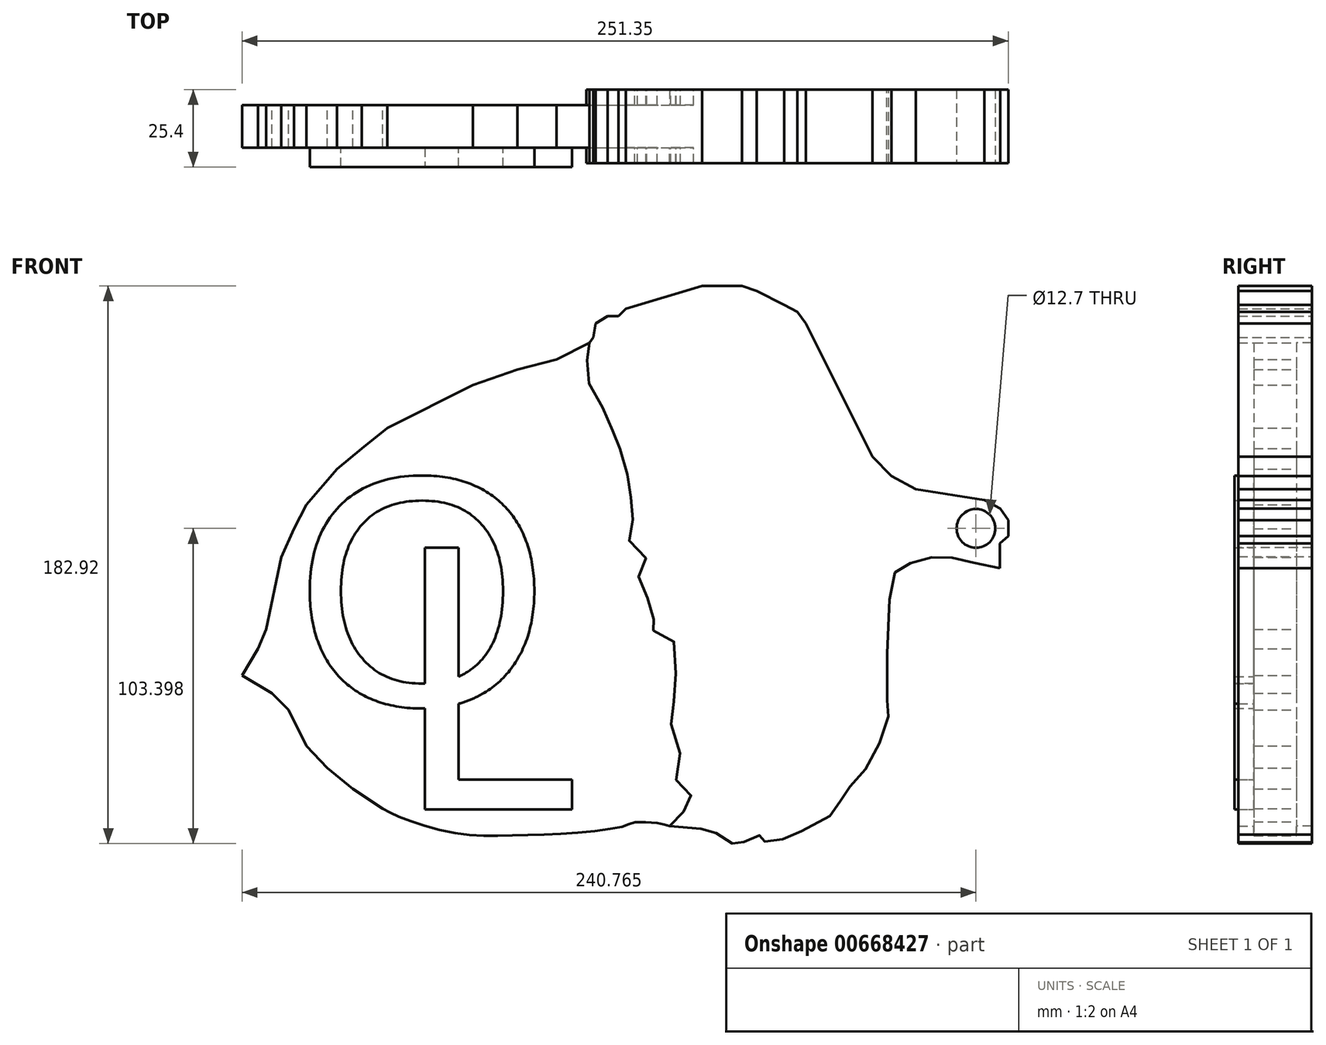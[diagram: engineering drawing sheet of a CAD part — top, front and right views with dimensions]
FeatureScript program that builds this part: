
annotation { "Feature Type Name" : "Feature", "Feature Type Description" : "" }
export const myFeature = defineFeature(function(context is Context, id is Id, definition is map)
    precondition{}
    {
        {
            var Q0;
            Q0=qCreatedBy(makeId("Front.planeOp"),FACE);
            var sketch = newSketch(context, id + "F0", { "sketchPlane" : qUnion([Q0])});
            skLineSegment(sketch, "E0", {"start": v(117.29, -24.43) * mm, "end": v(117.29, -16.31) * mm});
            skLineSegment(sketch, "E1", {"start": v(117.29, -16.31) * mm, "end": v(120, -13.9) * mm});
            skLineSegment(sketch, "E2", {"start": v(120, -13.9) * mm, "end": v(120, -8.7) * mm});
            skLineSegment(sketch, "E3", {"start": v(120, -8.7) * mm, "end": v(117.4, -4.81) * mm});
            skLineSegment(sketch, "E4", {"start": v(117.4, -4.81) * mm, "end": v(112.2, -2.02) * mm});
            skLineSegment(sketch, "E5", {"start": v(112.2, -2.02) * mm, "end": v(89.69, 1.5) * mm});
            skLineSegment(sketch, "E6", {"start": v(89.69, 1.5) * mm, "end": v(81.7, 5.78) * mm});
            skLineSegment(sketch, "E7", {"start": v(81.7, 5.78) * mm, "end": v(75.49, 12.18) * mm});
            skLineSegment(sketch, "E8", {"start": v(75.49, 12.18) * mm, "end": v(53.6, 55.9) * mm});
            skLineSegment(sketch, "E9", {"start": v(53.6, 55.9) * mm, "end": v(50.79, 59.7) * mm});
            skLineSegment(sketch, "E10", {"start": v(50.79, 59.7) * mm, "end": v(46.54, 62.01) * mm});
            skLineSegment(sketch, "E11", {"start": v(46.54, 62.01) * mm, "end": v(37.43, 66.54) * mm});
            skLineSegment(sketch, "E12", {"start": v(37.43, 66.54) * mm, "end": v(32.62, 68.17) * mm});
            skLineSegment(sketch, "E13", {"start": v(32.62, 68.17) * mm, "end": v(25.4, 68.17) * mm});
            skLineSegment(sketch, "E14", {"start": v(25.4, 68.17) * mm, "end": v(19.57, 68.17) * mm});
            skLineSegment(sketch, "E15", {"start": v(19.57, 68.17) * mm, "end": v(-5.42, 60.74) * mm});
            skLineSegment(sketch, "E16", {"start": v(-5.42, 60.74) * mm, "end": v(-7.89, 58.28) * mm});
            skLineSegment(sketch, "E17", {"start": v(-7.89, 58.28) * mm, "end": v(-11.38, 58.28) * mm});
            skLineSegment(sketch, "E18", {"start": v(-11.38, 58.28) * mm, "end": v(-15.33, 55.9) * mm});
            skLineSegment(sketch, "E19", {"start": v(-15.33, 55.9) * mm, "end": v(-16.06, 51.23) * mm});
            skLineSegment(sketch, "E20", {"start": v(-16.06, 51.23) * mm, "end": v(-17.41, 49.45) * mm});
            skLineSegment(sketch, "E21", {"start": v(-17.41, 49.45) * mm, "end": v(-24.9, 45.7) * mm});
            skLineSegment(sketch, "E22", {"start": v(-24.9, 45.7) * mm, "end": v(-28.14, 44.08) * mm});
            skLineSegment(sketch, "E23", {"start": v(-28.14, 44.08) * mm, "end": v(-40.96, 40.7) * mm});
            skLineSegment(sketch, "E24", {"start": v(-40.96, 40.7) * mm, "end": v(-55.61, 35.61) * mm});
            skLineSegment(sketch, "E25", {"start": v(-55.61, 35.61) * mm, "end": v(-66.58, 30.12) * mm});
            skLineSegment(sketch, "E26", {"start": v(-66.58, 30.12) * mm, "end": v(-75.74, 25.53) * mm});
            skLineSegment(sketch, "E27", {"start": v(-75.74, 25.53) * mm, "end": v(-83.63, 21.58) * mm});
            skLineSegment(sketch, "E28", {"start": v(-83.63, 21.58) * mm, "end": v(-92.03, 14.87) * mm});
            skLineSegment(sketch, "E29", {"start": v(-92.03, 14.87) * mm, "end": v(-100.15, 8.05) * mm});
            skLineSegment(sketch, "E30", {"start": v(-100.15, 8.05) * mm, "end": v(-110.16, -3.56) * mm});
            skLineSegment(sketch, "E31", {"start": v(-110.16, -3.56) * mm, "end": v(-114.23, -11.4) * mm});
            skLineSegment(sketch, "E32", {"start": v(-114.23, -11.4) * mm, "end": v(-118.43, -20.82) * mm});
            skLineSegment(sketch, "E33", {"start": v(-118.43, -20.82) * mm, "end": v(-123.37, -44.47) * mm});
            skLineSegment(sketch, "E34", {"start": v(-123.37, -44.47) * mm, "end": v(-126.12, -50.86) * mm});
            skLineSegment(sketch, "E35", {"start": v(-126.12, -50.86) * mm, "end": v(-131.35, -59.56) * mm});
            skLineSegment(sketch, "E36", {"start": v(-131.35, -59.56) * mm, "end": v(-121.57, -65.42) * mm});
            skLineSegment(sketch, "E37", {"start": v(-121.57, -65.42) * mm, "end": v(-116.11, -70.88) * mm});
            skLineSegment(sketch, "E38", {"start": v(-116.11, -70.88) * mm, "end": v(-110.16, -82.76) * mm});
            skLineSegment(sketch, "E39", {"start": v(-110.16, -82.76) * mm, "end": v(-103.34, -89.88) * mm});
            skLineSegment(sketch, "E40", {"start": v(-103.34, -89.88) * mm, "end": v(-94.93, -96.85) * mm});
            skLineSegment(sketch, "E41", {"start": v(-94.93, -96.85) * mm, "end": v(-85.2, -103.23) * mm});
            skFitSpline(sketch, "E42", {"points": [v(-85.2, -103.23) * mm, v(-78.53, -106.42) * mm, v(-60.98, -111.36) * mm, v(-44.15, -112.08) * mm, v(-22.53, -111.21) * mm, v(-5.7, -108.89) * mm, v(-2.36, -107.73) * mm, v(6.49, -108.3) * mm, v(8.96, -109.03) * mm, v(23.03, -110.34) * mm, v(23.76, -110.92) * mm, v(29.12, -114.55) * mm, v(30.57, -114.7) * mm, v(34.2, -113.97) * mm, v(38.4, -111.94) * mm, v(39.14, -111.94) * mm, v(40, -113.97) * mm, v(45.37, -113.53) * mm, v(51.9, -110.77) * mm, v(64.38, -103.23) * mm, v(64.96, -100.18) * mm, v(69.6, -94.53) * mm, v(75.99, -85.68) * mm, v(80.78, -72.47) * mm, v(80.46, -69.35) * mm, v(81.47, -30.75) * mm, v(84.08, -24.66) * mm, v(90.76, -21.76) * mm, v(98.6, -20.6) * mm, v(105.85, -21.9) * mm, v(117.29, -24.43) * mm], "startDerivative": vector(175.5, -94.23) * mm, "endDerivative": vector(297.3, -63.2) * mm});
            skFitSpline(sketch, "E43", {"points": [v(-17.41, 49.45) * mm, v(-17.41, 38.95) * mm, v(-13.96, 29.93) * mm, v(-10.06, 21.27) * mm, v(-8.33, 16.85) * mm, v(-5.5, 7.87) * mm, v(-4.08, 0) * mm, v(-3.31, -7) * mm, v(-3.61, -13.9) * mm, v(0, -20.63) * mm, v(0, -24.43) * mm, v(0, -30.75) * mm, v(3.3, -39.07) * mm, v(2.91, -43.7) * mm, v(6.62, -46.18) * mm, v(10.27, -55.88) * mm, v(10.24, -67.77) * mm, v(9.96, -75.4) * mm, v(11.82, -87.89) * mm, v(12.58, -95.6) * mm, v(14.74, -99.85) * mm, v(8.96, -109.03) * mm], "startDerivative": vector(-16.4, -195.96) * mm, "endDerivative": vector(-157.1, -181.16) * mm});
            skSolve(sketch);
        }
        {
            var Q0;
            Q0=makeQuery(id+"F0.imprint","IMPRINT",FACE,{"disambiguationData":[TD([[makeQuery(id+"F0.imprint","IMPRINT",EDGE,{"derivedFrom":sQuery(id+"F0.wireOp",EDGE,"E21")}),1.0]])]});
            extrude(context, id + "F1", {"entities" : qUnion([Q0]), "depth" : 12.7 * mm, "offsetDistance" : 25.4 * mm});
        }
        {
            var Q0;
            Q0 = qSketchRegion(id + "F0", true);
            var Q1;
            Q1=makeQuery(id+"F1.opExtrude","CAP_FACE",FACE,{"disambiguationData":[OSD([sQuery(id+"F0.wireOp",EDGE,"E21"),sQuery(id+"F0.wireOp",EDGE,"E22"),sQuery(id+"F0.wireOp",EDGE,"E23"),sQuery(id+"F0.wireOp",EDGE,"E24"),sQuery(id+"F0.wireOp",EDGE,"E25"),sQuery(id+"F0.wireOp",EDGE,"E26"),sQuery(id+"F0.wireOp",EDGE,"E27"),sQuery(id+"F0.wireOp",EDGE,"E28"),sQuery(id+"F0.wireOp",EDGE,"E29"),sQuery(id+"F0.wireOp",EDGE,"E30"),sQuery(id+"F0.wireOp",EDGE,"E31"),sQuery(id+"F0.wireOp",EDGE,"E32"),sQuery(id+"F0.wireOp",EDGE,"E33"),sQuery(id+"F0.wireOp",EDGE,"E34"),sQuery(id+"F0.wireOp",EDGE,"E35"),sQuery(id+"F0.wireOp",EDGE,"E36"),sQuery(id+"F0.wireOp",EDGE,"E37"),sQuery(id+"F0.wireOp",EDGE,"E38"),sQuery(id+"F0.wireOp",EDGE,"E39"),sQuery(id+"F0.wireOp",EDGE,"E40"),sQuery(id+"F0.wireOp",EDGE,"E41"),sQuery(id+"F0.wireOp",EDGE,"E42"),sQuery(id+"F0.wireOp",EDGE,"E43")])],"isStart":true});
            extrude(context, id + "F2", {"entities" : qUnion([Q0, Q1]), "operationType" : NewBodyOperationType.ADD, "depth" : 13.97 * mm, "offsetDistance" : 25.4 * mm});
        }
        {
            var Q0;
            Q0=makeQuery(id+"F2.opExtrude","CAP_FACE",FACE,{"disambiguationData":[OSD([sQuery(id+"F0.wireOp",EDGE,"E0"),sQuery(id+"F0.wireOp",EDGE,"E1"),sQuery(id+"F0.wireOp",EDGE,"E2"),sQuery(id+"F0.wireOp",EDGE,"E3"),sQuery(id+"F0.wireOp",EDGE,"E4"),sQuery(id+"F0.wireOp",EDGE,"E5"),sQuery(id+"F0.wireOp",EDGE,"E6"),sQuery(id+"F0.wireOp",EDGE,"E7"),sQuery(id+"F0.wireOp",EDGE,"E8"),sQuery(id+"F0.wireOp",EDGE,"E9"),sQuery(id+"F0.wireOp",EDGE,"E10"),sQuery(id+"F0.wireOp",EDGE,"E11"),sQuery(id+"F0.wireOp",EDGE,"E12"),sQuery(id+"F0.wireOp",EDGE,"E13"),sQuery(id+"F0.wireOp",EDGE,"E14"),sQuery(id+"F0.wireOp",EDGE,"E15"),sQuery(id+"F0.wireOp",EDGE,"E16"),sQuery(id+"F0.wireOp",EDGE,"E17"),sQuery(id+"F0.wireOp",EDGE,"E18"),sQuery(id+"F0.wireOp",EDGE,"E19"),sQuery(id+"F0.wireOp",EDGE,"E20"),sQuery(id+"F0.wireOp",EDGE,"E21"),sQuery(id+"F0.wireOp",EDGE,"E22"),sQuery(id+"F0.wireOp",EDGE,"E23"),sQuery(id+"F0.wireOp",EDGE,"E24"),sQuery(id+"F0.wireOp",EDGE,"E25"),sQuery(id+"F0.wireOp",EDGE,"E26"),sQuery(id+"F0.wireOp",EDGE,"E27"),sQuery(id+"F0.wireOp",EDGE,"E28"),sQuery(id+"F0.wireOp",EDGE,"E29"),sQuery(id+"F0.wireOp",EDGE,"E30"),sQuery(id+"F0.wireOp",EDGE,"E31"),sQuery(id+"F0.wireOp",EDGE,"E32"),sQuery(id+"F0.wireOp",EDGE,"E33"),sQuery(id+"F0.wireOp",EDGE,"E34"),sQuery(id+"F0.wireOp",EDGE,"E35"),sQuery(id+"F0.wireOp",EDGE,"E36"),sQuery(id+"F0.wireOp",EDGE,"E37"),sQuery(id+"F0.wireOp",EDGE,"E38"),sQuery(id+"F0.wireOp",EDGE,"E39"),sQuery(id+"F0.wireOp",EDGE,"E40"),sQuery(id+"F0.wireOp",EDGE,"E41"),sQuery(id+"F0.wireOp",EDGE,"E42")])],"isStart":false});
            var sketch = newSketch(context, id + "F3", { "sketchPlane" : qUnion([Q0])});
            skFitSpline(sketch, "E44.0", {"points": [v(-17.41, 49.45) * mm, v(-17.72, 45.83) * mm, v(-18.3, 38.74) * mm, v(-14.01, 30.22) * mm, v(-10, 21.22) * mm, v(-8.33, 16.97) * mm, v(-5.13, 7.74) * mm, v(-4.22, 0.14) * mm, v(-2.66, -6.98) * mm, v(-5.07, -14.01) * mm, v(0.85, -20.43) * mm, v(-0.06, -24.46) * mm, v(-1.11, -31.07) * mm, v(4.78, -38.55) * mm, v(1.48, -44.4) * mm, v(8.05, -45.44) * mm, v(10.95, -56.12) * mm, v(10.37, -67.84) * mm, v(9.33, -75.26) * mm, v(12.48, -87.68) * mm, v(11.46, -95.7) * mm, v(16.8, -99.98) * mm, v(11.9, -105.63) * mm, v(8.96, -109.03) * mm]});
            skSolve(sketch);
        }
        {
            var Q0;
            {var subQ0=sQuery(id+"F0.wireOp",EDGE,"E42");var subQ1=sQuery(id+"F0.wireOp",EDGE,"E41");var subQ2=sQuery(id+"F0.wireOp",EDGE,"E40");var subQ3=sQuery(id+"F0.wireOp",EDGE,"E39");var subQ4=sQuery(id+"F0.wireOp",EDGE,"E38");var subQ5=sQuery(id+"F0.wireOp",EDGE,"E37");var subQ6=sQuery(id+"F0.wireOp",EDGE,"E36");var subQ7=sQuery(id+"F0.wireOp",EDGE,"E35");var subQ8=sQuery(id+"F0.wireOp",EDGE,"E34");var subQ9=sQuery(id+"F0.wireOp",EDGE,"E33");var subQ10=sQuery(id+"F0.wireOp",EDGE,"E32");var subQ11=sQuery(id+"F0.wireOp",EDGE,"E31");var subQ12=sQuery(id+"F0.wireOp",EDGE,"E30");var subQ13=sQuery(id+"F0.wireOp",EDGE,"E29");var subQ14=sQuery(id+"F0.wireOp",EDGE,"E28");var subQ15=sQuery(id+"F0.wireOp",EDGE,"E27");var subQ16=sQuery(id+"F0.wireOp",EDGE,"E26");var subQ17=sQuery(id+"F0.wireOp",EDGE,"E25");var subQ18=sQuery(id+"F0.wireOp",EDGE,"E24");var subQ19=sQuery(id+"F0.wireOp",EDGE,"E23");var subQ20=sQuery(id+"F0.wireOp",EDGE,"E22");var subQ21=sQuery(id+"F0.wireOp",EDGE,"E21");Q0=makeQuery(id+"F2.boolean.opBoolean","MERGE",FACE,{"derivedFrom":[makeQuery(id+"F1.opExtrude","CAP_FACE",FACE,{"disambiguationData":[OSD([subQ21,subQ20,subQ19,subQ18,subQ17,subQ16,subQ15,subQ14,subQ13,subQ12,subQ11,subQ10,subQ9,subQ8,subQ7,subQ6,subQ5,subQ4,subQ3,subQ2,subQ1,subQ0,sQuery(id+"F0.wireOp",EDGE,"E43")])],"isStart":true}),makeQuery(id+"F2.opExtrude","CAP_FACE",FACE,{"disambiguationData":[OSD([sQuery(id+"F0.wireOp",EDGE,"E0"),sQuery(id+"F0.wireOp",EDGE,"E1"),sQuery(id+"F0.wireOp",EDGE,"E2"),sQuery(id+"F0.wireOp",EDGE,"E3"),sQuery(id+"F0.wireOp",EDGE,"E4"),sQuery(id+"F0.wireOp",EDGE,"E5"),sQuery(id+"F0.wireOp",EDGE,"E6"),sQuery(id+"F0.wireOp",EDGE,"E7"),sQuery(id+"F0.wireOp",EDGE,"E8"),sQuery(id+"F0.wireOp",EDGE,"E9"),sQuery(id+"F0.wireOp",EDGE,"E10"),sQuery(id+"F0.wireOp",EDGE,"E11"),sQuery(id+"F0.wireOp",EDGE,"E12"),sQuery(id+"F0.wireOp",EDGE,"E13"),sQuery(id+"F0.wireOp",EDGE,"E14"),sQuery(id+"F0.wireOp",EDGE,"E15"),sQuery(id+"F0.wireOp",EDGE,"E16"),sQuery(id+"F0.wireOp",EDGE,"E17"),sQuery(id+"F0.wireOp",EDGE,"E18"),sQuery(id+"F0.wireOp",EDGE,"E19"),sQuery(id+"F0.wireOp",EDGE,"E20"),subQ21,subQ20,subQ19,subQ18,subQ17,subQ16,subQ15,subQ14,subQ13,subQ12,subQ11,subQ10,subQ9,subQ8,subQ7,subQ6,subQ5,subQ4,subQ3,subQ2,subQ1,subQ0])],"isStart":true})]});}
            var sketch = newSketch(context, id + "F4", { "sketchPlane" : qUnion([Q0])});
            skFitSpline(sketch, "E45.0", {"points": [v(17.41, 49.45) * mm, v(17.72, 45.83) * mm, v(18.3, 38.74) * mm, v(14.01, 30.22) * mm, v(10, 21.22) * mm, v(8.33, 16.97) * mm, v(5.13, 7.74) * mm, v(4.22, 0.14) * mm, v(2.66, -6.98) * mm, v(5.07, -14.01) * mm, v(-0.85, -20.43) * mm, v(0.06, -24.46) * mm, v(1.11, -31.07) * mm, v(-4.78, -38.55) * mm, v(-1.48, -44.4) * mm, v(-8.05, -45.44) * mm, v(-10.95, -56.12) * mm, v(-10.37, -67.84) * mm, v(-9.33, -75.26) * mm, v(-12.48, -87.68) * mm, v(-11.46, -95.7) * mm, v(-16.8, -99.98) * mm, v(-11.9, -105.63) * mm, v(-8.96, -109.03) * mm]});
            skSolve(sketch);
        }
        {
            var Q0;
            {var subQ0=sQuery(id+"F3.wireOp",EDGE,"E44.0");Q0=makeQuery(id+"F3.imprint","IMPRINT",FACE,{"disambiguationData":[TD([[makeQuery(id+"F3.imprint","IMPRINT",EDGE,{"derivedFrom":subQ0}),1.0]])]});}
            extrude(context, id + "F5", {"entities" : qUnion([Q0]), "operationType" : NewBodyOperationType.ADD, "depth" : 5.08 * mm, "offsetDistance" : 25.4 * mm});
        }
        {
            var Q0;
            {var subQ0=sQuery(id+"F4.wireOp",EDGE,"E45.0");Q0=makeQuery(id+"F4.imprint","IMPRINT",FACE,{"disambiguationData":[TD([[makeQuery(id+"F4.imprint","IMPRINT",EDGE,{"derivedFrom":subQ0}),-1.0]])]});}
            extrude(context, id + "F6", {"entities" : qUnion([Q0]), "operationType" : NewBodyOperationType.ADD, "depth" : 5.08 * mm, "offsetDistance" : 25.4 * mm});
        }
        {
            var Q0;
            Q0=makeQuery(id+"F2.opExtrude","CAP_FACE",FACE,{"disambiguationData":[OSD([sQuery(id+"F0.wireOp",EDGE,"E0"),sQuery(id+"F0.wireOp",EDGE,"E1"),sQuery(id+"F0.wireOp",EDGE,"E2"),sQuery(id+"F0.wireOp",EDGE,"E3"),sQuery(id+"F0.wireOp",EDGE,"E4"),sQuery(id+"F0.wireOp",EDGE,"E5"),sQuery(id+"F0.wireOp",EDGE,"E6"),sQuery(id+"F0.wireOp",EDGE,"E7"),sQuery(id+"F0.wireOp",EDGE,"E8"),sQuery(id+"F0.wireOp",EDGE,"E9"),sQuery(id+"F0.wireOp",EDGE,"E10"),sQuery(id+"F0.wireOp",EDGE,"E11"),sQuery(id+"F0.wireOp",EDGE,"E12"),sQuery(id+"F0.wireOp",EDGE,"E13"),sQuery(id+"F0.wireOp",EDGE,"E14"),sQuery(id+"F0.wireOp",EDGE,"E15"),sQuery(id+"F0.wireOp",EDGE,"E16"),sQuery(id+"F0.wireOp",EDGE,"E17"),sQuery(id+"F0.wireOp",EDGE,"E18"),sQuery(id+"F0.wireOp",EDGE,"E19"),sQuery(id+"F0.wireOp",EDGE,"E20"),sQuery(id+"F0.wireOp",EDGE,"E21"),sQuery(id+"F0.wireOp",EDGE,"E22"),sQuery(id+"F0.wireOp",EDGE,"E23"),sQuery(id+"F0.wireOp",EDGE,"E24"),sQuery(id+"F0.wireOp",EDGE,"E25"),sQuery(id+"F0.wireOp",EDGE,"E26"),sQuery(id+"F0.wireOp",EDGE,"E27"),sQuery(id+"F0.wireOp",EDGE,"E28"),sQuery(id+"F0.wireOp",EDGE,"E29"),sQuery(id+"F0.wireOp",EDGE,"E30"),sQuery(id+"F0.wireOp",EDGE,"E31"),sQuery(id+"F0.wireOp",EDGE,"E32"),sQuery(id+"F0.wireOp",EDGE,"E33"),sQuery(id+"F0.wireOp",EDGE,"E34"),sQuery(id+"F0.wireOp",EDGE,"E35"),sQuery(id+"F0.wireOp",EDGE,"E36"),sQuery(id+"F0.wireOp",EDGE,"E37"),sQuery(id+"F0.wireOp",EDGE,"E38"),sQuery(id+"F0.wireOp",EDGE,"E39"),sQuery(id+"F0.wireOp",EDGE,"E40"),sQuery(id+"F0.wireOp",EDGE,"E41"),sQuery(id+"F0.wireOp",EDGE,"E42")])],"isStart":false});
            var sketch = newSketch(context, id + "F7", { "sketchPlane" : qUnion([Q0])});
            skText(sketch, "E46", { "text": "O", "fontName": "Arimo-Regular.ttf"});
            const initialGuessF7  = {"E46": [-0.11423, -0.06936, 1, 0, 0.07769]};
            skSetInitialGuess(sketch, initialGuessF7);
            skSolve(sketch);
        }
        {
            var Q0;
            Q0=makeQuery(id+"F7.imprint","IMPRINT",FACE,{"disambiguationData":[TD([[makeQuery(id+"F7.imprint","IMPRINT",EDGE,{"derivedFrom":sQuery(id+"F7.wireOp",EDGE,"E46.sketch_text.stroke-0")}),1.0]])]});
            var sketch = newSketch(context, id + "F8", { "sketchPlane" : qUnion([Q0])});
            skText(sketch, "E47", { "text": "L", "fontName": "DroidSansMono.ttf"});
            const initialGuessF8  = {"E47": [-0.08498, -0.10348, 1, 0, 0.08649]};
            skSetInitialGuess(sketch, initialGuessF8);
            skSolve(sketch);
        }
        {
            var Q0;
            Q0 = qSketchRegion(id + "F7", true);
            var Q1;
            Q1 = qSketchRegion(id + "F8", true);
            extrude(context, id + "F9", {"entities" : qUnion([Q0, Q1]), "operationType" : NewBodyOperationType.ADD, "depth" : 6.35 * mm, "offsetDistance" : 25.4 * mm});
        }
        {
            var Q0;
            Q0=makeQuery(id+"F5.opExtrude","CAP_FACE",FACE,{"disambiguationData":[OSD([sQuery(id+"F0.wireOp",EDGE,"E0"),sQuery(id+"F0.wireOp",EDGE,"E1"),sQuery(id+"F0.wireOp",EDGE,"E2"),sQuery(id+"F0.wireOp",EDGE,"E3"),sQuery(id+"F0.wireOp",EDGE,"E4"),sQuery(id+"F0.wireOp",EDGE,"E5"),sQuery(id+"F0.wireOp",EDGE,"E6"),sQuery(id+"F0.wireOp",EDGE,"E7"),sQuery(id+"F0.wireOp",EDGE,"E8"),sQuery(id+"F0.wireOp",EDGE,"E9"),sQuery(id+"F0.wireOp",EDGE,"E10"),sQuery(id+"F0.wireOp",EDGE,"E11"),sQuery(id+"F0.wireOp",EDGE,"E12"),sQuery(id+"F0.wireOp",EDGE,"E13"),sQuery(id+"F0.wireOp",EDGE,"E14"),sQuery(id+"F0.wireOp",EDGE,"E15"),sQuery(id+"F0.wireOp",EDGE,"E16"),sQuery(id+"F0.wireOp",EDGE,"E17"),sQuery(id+"F0.wireOp",EDGE,"E18"),sQuery(id+"F0.wireOp",EDGE,"E19"),sQuery(id+"F0.wireOp",EDGE,"E20"),sQuery(id+"F0.wireOp",EDGE,"E42"),sQuery(id+"F3.wireOp",EDGE,"E44.0")])],"isStart":false});
            var sketch = newSketch(context, id + "F10", { "sketchPlane" : qUnion([Q0])});
            skCircle(sketch, "E48", {"center": v(109.42, -11.35) * mm, "radius": 6.35 * mm});
            skSolve(sketch);
        }
        {
            var Q0;
            Q0 = qSketchRegion(id + "F10", true);
            extrude(context, id + "F11", {"entities" : qUnion([Q0]), "operationType" : NewBodyOperationType.REMOVE, "oppositeDirection" : true, "depth" : 25.4 * mm, "offsetDistance" : 25.4 * mm});
        }
    });
